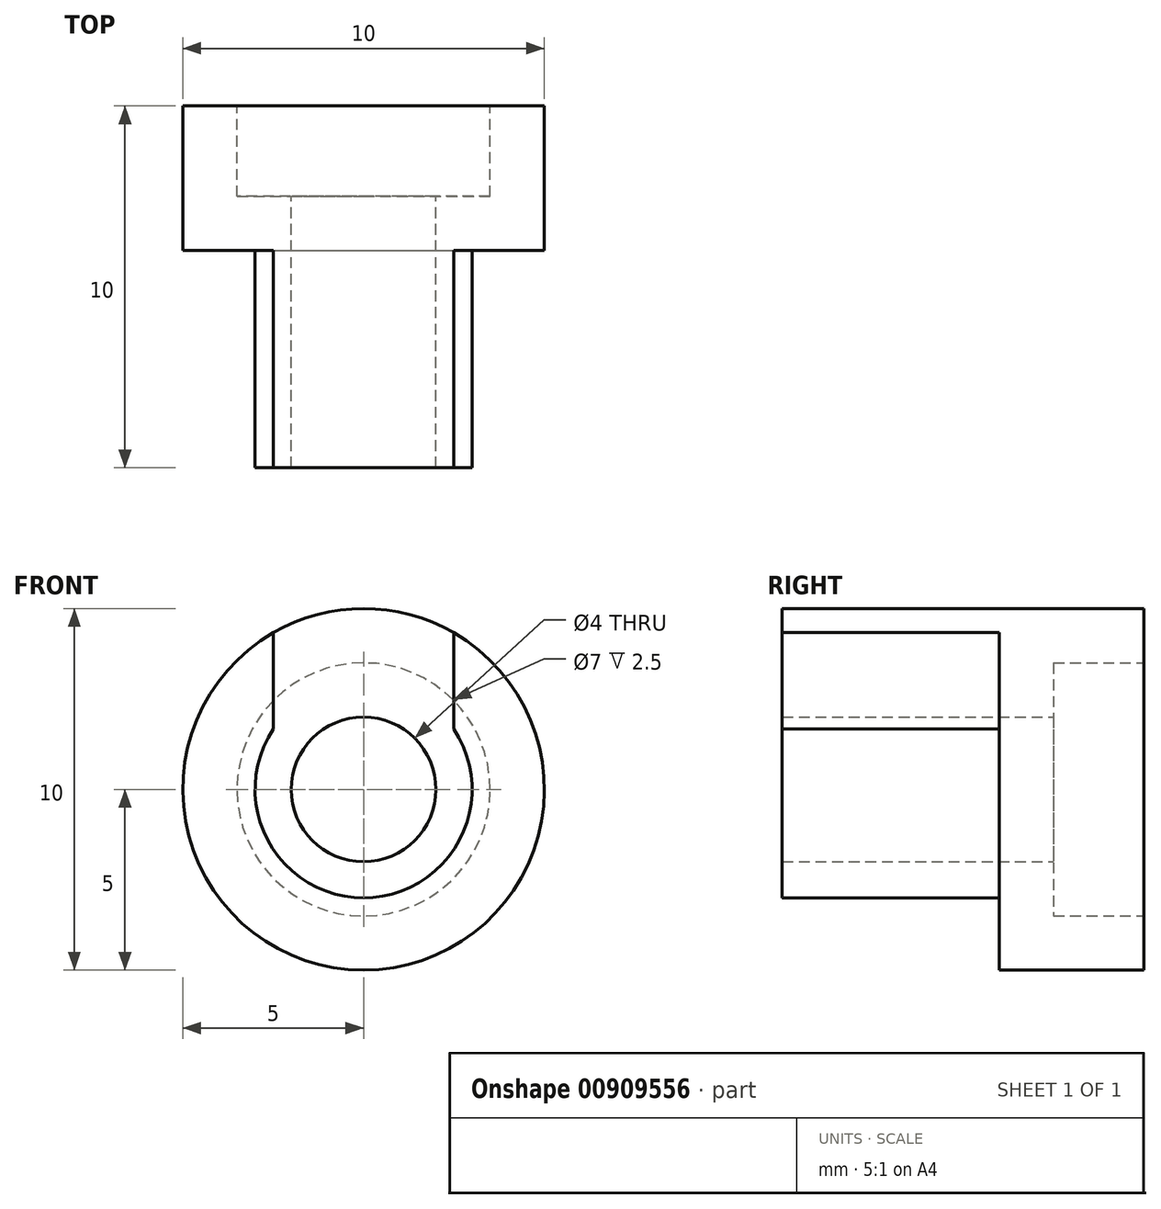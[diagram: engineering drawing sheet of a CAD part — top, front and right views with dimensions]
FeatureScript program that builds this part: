
annotation { "Feature Type Name" : "Feature", "Feature Type Description" : "" }
export const myFeature = defineFeature(function(context is Context, id is Id, definition is map)
    precondition{}
    {
        {
            var Q0;
            Q0=qCreatedBy(makeId("Front.planeOp"),FACE);
            var sketch = newSketch(context, id + "F0", { "sketchPlane" : qUnion([Q0])});
            skCircle(sketch, "E0", {"center": v(0, 0) * mm, "radius": 5 * mm});
            skSolve(sketch);
        }
        {
            var Q0;
            Q0=makeQuery(id+"F0.imprint","IMPRINT",FACE,{"disambiguationData":[TD([[makeQuery(id+"F0.imprint","IMPRINT",EDGE,{"derivedFrom":sQuery(id+"F0.wireOp",EDGE,"E0")}),1.0]])]});
            extrude(context, id + "F1", {"entities" : qUnion([Q0]), "depth" : 4 * mm, "offsetDistance" : 25 * mm});
        }
        {
            var Q0;
            Q0=makeQuery(id+"F1.opExtrude","CAP_FACE",FACE,{"disambiguationData":[OSD([sQuery(id+"F0.wireOp",EDGE,"E0")])],"isStart":false});
            var sketch = newSketch(context, id + "F2", { "sketchPlane" : qUnion([Q0])});
            skCircle(sketch, "E1", {"center": v(0, 0) * mm, "radius": 3 * mm});
            skSolve(sketch);
        }
        {
            var Q0;
            Q0=makeQuery(id+"F2.imprint","IMPRINT",FACE,{"disambiguationData":[TD([[makeQuery(id+"F2.imprint","IMPRINT",EDGE,{"derivedFrom":sQuery(id+"F2.wireOp",EDGE,"E1")}),1.0]])]});
            extrude(context, id + "F3", {"entities" : qUnion([Q0]), "operationType" : NewBodyOperationType.ADD, "depth" : 6 * mm, "offsetDistance" : 25 * mm});
        }
        {
            var Q0;
            Q0=makeQuery(id+"F1.opExtrude","CAP_FACE",FACE,{"disambiguationData":[OSD([sQuery(id+"F0.wireOp",EDGE,"E0")])],"isStart":true});
            var sketch = newSketch(context, id + "F4", { "sketchPlane" : qUnion([Q0])});
            skCircle(sketch, "E2", {"center": v(0, 0) * mm, "radius": 2 * mm});
            skCircle(sketch, "E3", {"center": v(0, 0) * mm, "radius": 3.5 * mm});
            skSolve(sketch);
        }
        {
            var Q0;
            Q0=makeQuery(id+"F4.imprint","IMPRINT",FACE,{"disambiguationData":[TD([[makeQuery(id+"F4.imprint","IMPRINT",EDGE,{"derivedFrom":sQuery(id+"F4.wireOp",EDGE,"E2")}),1.0]])]});
            extrude(context, id + "F5", {"entities" : qUnion([Q0]), "operationType" : NewBodyOperationType.REMOVE, "oppositeDirection" : true, "depth" : 25 * mm, "offsetDistance" : 25 * mm});
        }
        {
            var Q0;
            Q0=makeQuery(id+"F4.imprint","IMPRINT",FACE,{"disambiguationData":[TD([[makeQuery(id+"F4.imprint","IMPRINT",EDGE,{"derivedFrom":sQuery(id+"F4.wireOp",EDGE,"E2")}),-1.0]])]});
            extrude(context, id + "F6", {"entities" : qUnion([Q0]), "operationType" : NewBodyOperationType.REMOVE, "oppositeDirection" : true, "depth" : 2.5 * mm, "offsetDistance" : 25 * mm});
        }
        {
            var Q0;
            Q0=makeQuery(id+"F3.opExtrude","CAP_FACE",FACE,{"disambiguationData":[OSD([sQuery(id+"F2.wireOp",EDGE,"E1")])],"isStart":false});
            var sketch = newSketch(context, id + "F7", { "sketchPlane" : qUnion([Q0])});
            skArc(sketch, "E4", {"start": v(2.5, 4.33) * mm, "mid": v(0, 5) * mm, "end": v(-2.5, 4.33) * mm});
            skLineSegment(sketch, "E5", {"start": v(-2.5, 1.67) * mm, "end": v(-2.5, 4.33) * mm});
            skLineSegment(sketch, "E6", {"start": v(2.5, 1.67) * mm, "end": v(2.5, 4.33) * mm});
            skArc(sketch, "E7", {"start": v(2.5, 1.67) * mm, "mid": v(0, 3) * mm, "end": v(-2.5, 1.67) * mm});
            skSolve(sketch);
        }
        {
            var Q0;
            Q0=makeQuery(id+"F7.imprint","IMPRINT",FACE,{"disambiguationData":[TD([[makeQuery(id+"F7.imprint","IMPRINT",EDGE,{"derivedFrom":sQuery(id+"F7.wireOp",EDGE,"E4")}),1.0]])]});
            extrude(context, id + "F8", {"entities" : qUnion([Q0]), "operationType" : NewBodyOperationType.ADD, "oppositeDirection" : true, "depth" : 7 * mm, "offsetDistance" : 25 * mm});
        }
    });
